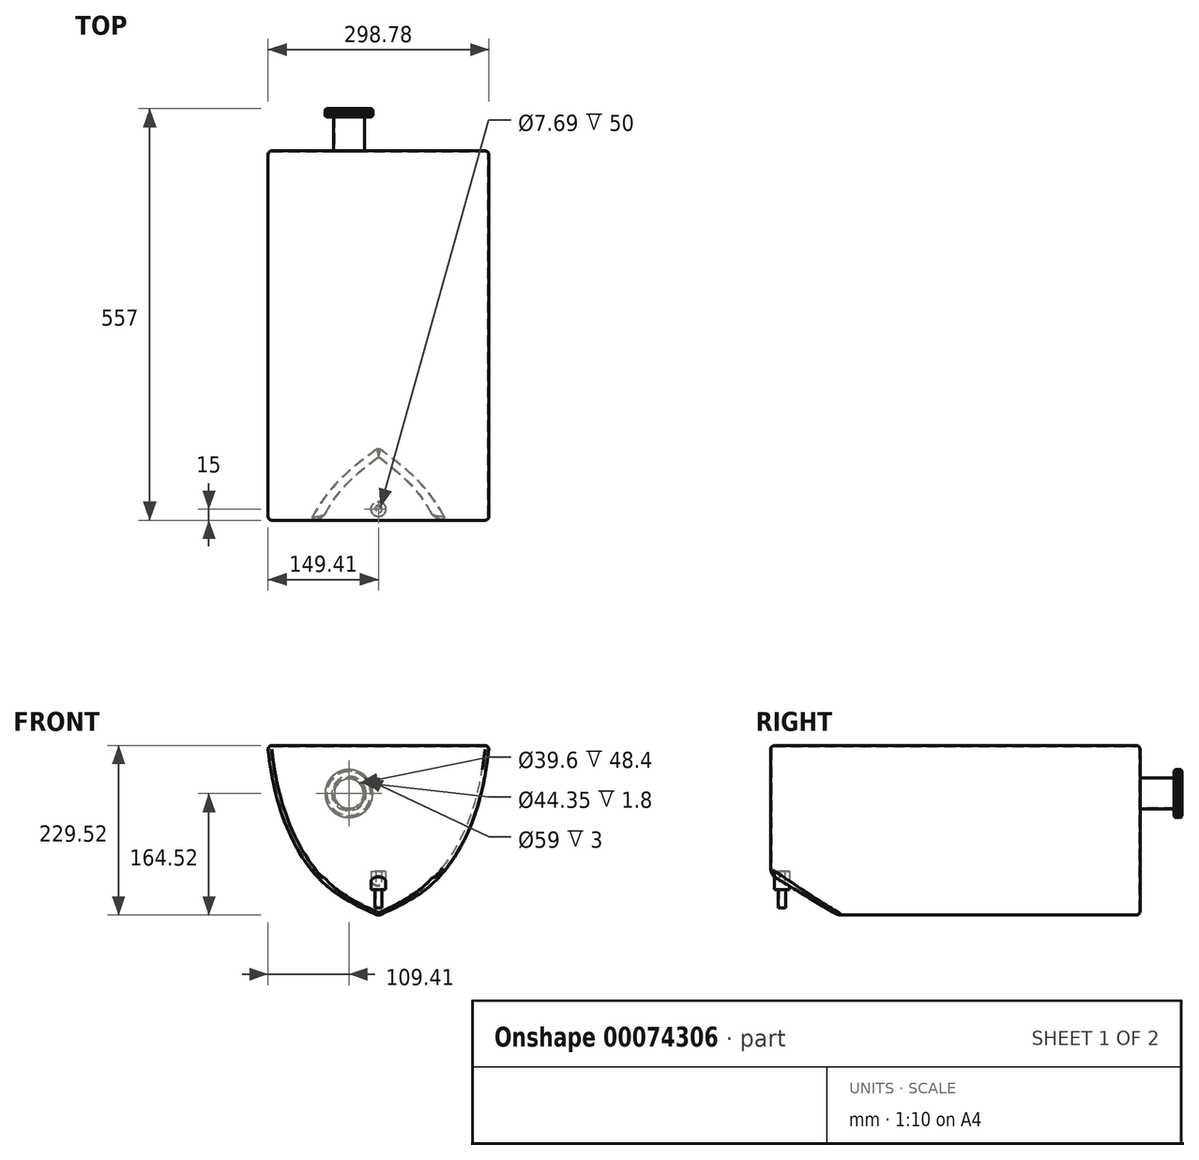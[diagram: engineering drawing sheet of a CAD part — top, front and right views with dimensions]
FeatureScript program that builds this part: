
annotation { "Feature Type Name" : "Feature", "Feature Type Description" : "" }
export const myFeature = defineFeature(function(context is Context, id is Id, definition is map)
    precondition{}
    {
        {
            var Q0;
            Q0=qCreatedBy(makeId("Front.planeOp"),FACE);
            var sketch = newSketch(context, id + "F0", { "sketchPlane" : qUnion([Q0])});
            skLineSegment(sketch, "E0", {"start": v(0, 0) * mm, "end": v(150, 0) * mm});
            skLineSegment(sketch, "E1", {"start": v(0, 0) * mm, "end": v(0, -230) * mm, "construction": true});
            skLineSegment(sketch, "E2", {"start": v(0, 0) * mm, "end": v(-150, 0) * mm});
            skLineSegment(sketch, "E3", {"start": v(-142.5, -50) * mm, "end": v(142.5, -50) * mm, "construction": true});
            skLineSegment(sketch, "E4", {"start": v(-120, -120) * mm, "end": v(120, -120) * mm, "construction": true});
            skLineSegment(sketch, "E5", {"start": v(-70, -190) * mm, "end": v(70, -190) * mm, "construction": true});
            skFitSpline(sketch, "E6", {"points": [v(0, -230) * mm, v(-70, -190) * mm, v(-120, -120) * mm, v(-142.5, -50) * mm, v(-150, 0) * mm], "startDerivative": vector(-280.35, 125.73) * mm, "endDerivative": vector(-29.97, 273.24) * mm});
            skFitSpline(sketch, "E7", {"points": [v(150, 0) * mm, v(142.5, -50) * mm, v(120, -120) * mm, v(70, -190) * mm, v(0, -230) * mm], "startDerivative": vector(-27.4, -229.65) * mm, "endDerivative": vector(-280.35, -125.73) * mm});
            skSolve(sketch);
        }
        {
            var Q0;
            Q0 = qSketchRegion(id + "F0", true);
            var Q1;
            Q1=makeQuery(id+"F0.imprint","IMPRINT",FACE,{"disambiguationData":[TD([[makeQuery(id+"F0.imprint","IMPRINT",EDGE,{"derivedFrom":sQuery(id+"F0.wireOp",EDGE,"E0")}),-1.0]])]});
            extrude(context, id + "F1", {"entities" : qUnion([Q0, Q1]), "depth" : 500 * mm});
        }
        {
            var Q0;
            Q0=makeQuery(id+"F1.opExtrude","CAP_EDGE",EDGE,{"disambiguationData":[OSD([sQuery(id+"F0.wireOp",EDGE,"E7")])],"isStart":true});
            var Q1;
            Q1=makeQuery(id+"F1.opExtrude","CAP_EDGE",EDGE,{"disambiguationData":[OSD([sQuery(id+"F0.wireOp",EDGE,"E6")])],"isStart":true});
            var Q2;
            Q2=makeQuery(id+"F1.opExtrude","SWEPT_EDGE",EDGE,{"disambiguationData":[OSD([sQuery(id+"F0.wireOp",EDGE,"E6"),sQuery(id+"F0.wireOp",EDGE,"E7")])]});
            var Q3;
            Q3=makeQuery(id+"F1.opExtrude","SWEPT_EDGE",EDGE,{"disambiguationData":[OSD([sQuery(id+"F0.wireOp",EDGE,"E2"),sQuery(id+"F0.wireOp",EDGE,"E6")])]});
            var Q4;
            Q4=makeQuery(id+"F1.opExtrude","CAP_EDGE",EDGE,{"disambiguationData":[OSD([sQuery(id+"F0.wireOp",EDGE,"E0"),sQuery(id+"F0.wireOp",EDGE,"E2")])],"isStart":true});
            var Q5;
            Q5=makeQuery(id+"F1.opExtrude","CAP_EDGE",EDGE,{"disambiguationData":[OSD([sQuery(id+"F0.wireOp",EDGE,"E7")])],"isStart":false});
            var Q6;
            Q6=makeQuery(id+"F1.opExtrude","CAP_EDGE",EDGE,{"disambiguationData":[OSD([sQuery(id+"F0.wireOp",EDGE,"E6")])],"isStart":false});
            var Q7;
            Q7=makeQuery(id+"F1.opExtrude","CAP_EDGE",EDGE,{"disambiguationData":[OSD([sQuery(id+"F0.wireOp",EDGE,"E0"),sQuery(id+"F0.wireOp",EDGE,"E2")])],"isStart":false});
            var Q8;
            Q8=makeQuery(id+"F1.opExtrude","SWEPT_EDGE",EDGE,{"disambiguationData":[OSD([sQuery(id+"F0.wireOp",EDGE,"E0"),sQuery(id+"F0.wireOp",EDGE,"E7")])]});
            fillet(context, id + "F2", {"entities" : qUnion([Q0, Q1, Q2, Q3, Q4, Q5, Q6, Q7, Q8]), "radius" : 5 * mm, "tangentPropagation" : true, "allowEdgeOverflow" : false});
        }
        {
            var Q0;
            Q0=makeQuery(id+"F0.imprint","IMPRINT",FACE,{"disambiguationData":[TD([[makeQuery(id+"F0.imprint","IMPRINT",EDGE,{"derivedFrom":sQuery(id+"F0.wireOp",EDGE,"E0")}),-1.0]])]});
            var sketch = newSketch(context, id + "F3", { "sketchPlane" : qUnion([Q0])});
            skCircle(sketch, "E8", {"center": v(-40, -65) * mm, "radius": 21 * mm});
            skSolve(sketch);
        }
        {
            var Q0;
            Q0 = qSketchRegion(id + "F3", true);
            extrude(context, id + "F4", {"entities" : qUnion([Q0]), "operationType" : NewBodyOperationType.ADD, "oppositeDirection" : true, "depth" : 46 * mm});
        }
        {
            var Q0;
            Q0=makeQuery(id+"F4.opExtrude","CAP_FACE",FACE,{"disambiguationData":[OSD([sQuery(id+"F3.wireOp",EDGE,"E8")])],"isStart":false});
            var sketch = newSketch(context, id + "F5", { "sketchPlane" : qUnion([Q0])});
            skCircle(sketch, "E9", {"center": v(40, -65) * mm, "radius": 23.38 * mm});
            skSolve(sketch);
        }
        {
            var Q0;
            Q0 = qSketchRegion(id + "F5", true);
            extrude(context, id + "F6", {"entities" : qUnion([Q0]), "operationType" : NewBodyOperationType.ADD, "depth" : 3 * mm});
        }
        {
            var Q0;
            Q0=qCreatedBy(makeId("Right.planeOp"),FACE);
            var sketch = newSketch(context, id + "F7", { "sketchPlane" : qUnion([Q0])});
            skLineSegment(sketch, "E10", {"start": v(-506.14, -175) * mm, "end": v(-466.14, -175) * mm, "construction": true});
            skLineSegment(sketch, "E11.2", {"start": v(-495, -229.08) * mm, "end": v(-5, -229.08) * mm, "construction": true});
            skFitSpline(sketch, "E12.1", {"points": [v(-500, -224.52) * mm, v(-500, -151.35) * mm, v(-500, -78.17) * mm, v(-500, -5) * mm], "construction": true});
            skLineSegment(sketch, "E13", {"start": v(-410, -168.35) * mm, "end": v(-410, -263.65) * mm, "construction": true});
            skLineSegment(sketch, "E14", {"start": v(-500, -175) * mm, "end": v(-410, -229.08) * mm});
            skLineSegment(sketch, "E15", {"start": v(-410, -229.08) * mm, "end": v(-412.5, -274.64) * mm});
            skLineSegment(sketch, "E16", {"start": v(-412.5, -274.64) * mm, "end": v(-520.63, -288.08) * mm});
            skLineSegment(sketch, "E17", {"start": v(-520.63, -288.08) * mm, "end": v(-500, -175) * mm});
            skSolve(sketch);
        }
        {
            var Q0;
            Q0 = qSketchRegion(id + "F7", true);
            extrude(context, id + "F8", {"entities" : qUnion([Q0]), "operationType" : NewBodyOperationType.REMOVE, "oppositeDirection" : true, "depth" : 500 * mm, "symmetric" : true});
        }
        {
            var Q0;
            Q0=makeQuery(id+"F8.boolean.opBoolean","INTERSECT",EDGE,{"derivedFrom":[makeQuery(id+"F1.opExtrude","SWEPT_FACE",FACE,{"disambiguationData":[OSD([sQuery(id+"F0.wireOp",EDGE,"E7")])]}),makeQuery(id+"F8.opExtrude","SWEPT_FACE",FACE,{"disambiguationData":[OSD([sQuery(id+"F7.wireOp",EDGE,"E14")])]})]});
            var Q1;
            Q1=makeQuery(id+"F8.boolean.opBoolean","INTERSECT",EDGE,{"derivedFrom":[makeQuery(id+"F1.opExtrude","SWEPT_FACE",FACE,{"disambiguationData":[OSD([sQuery(id+"F0.wireOp",EDGE,"E6")])]}),makeQuery(id+"F8.opExtrude","SWEPT_FACE",FACE,{"disambiguationData":[OSD([sQuery(id+"F7.wireOp",EDGE,"E14")])]})]});
            var Q2;
            Q2=makeQuery(id+"F8.boolean.opBoolean","COPY",EDGE,{"derivedFrom":makeQuery(id+"F8.opExtrude","SWEPT_EDGE",EDGE,{"disambiguationData":[OSD([sQuery(id+"F7.wireOp",EDGE,"E14"),sQuery(id+"F7.wireOp",EDGE,"E17")])]})});
            var Q3;
            Q3=makeQuery(id+"F8.boolean.opBoolean","COPY",EDGE,{"derivedFrom":makeQuery(id+"F8.opExtrude","SWEPT_EDGE",EDGE,{"disambiguationData":[OSD([sQuery(id+"F7.wireOp",EDGE,"E14"),sQuery(id+"F7.wireOp",EDGE,"E15")])]})});
            fillet(context, id + "F9", {"entities" : qUnion([Q0, Q1, Q2, Q3]), "radius" : 15 * mm, "tangentPropagation" : true, "allowEdgeOverflow" : false});
        }
        {
            var Q0;
            Q0=makeQuery(id+"F1.opExtrude","SWEPT_FACE",FACE,{"disambiguationData":[OSD([sQuery(id+"F0.wireOp",EDGE,"E0"),sQuery(id+"F0.wireOp",EDGE,"E2")])]});
            var sketch = newSketch(context, id + "F10", { "sketchPlane" : qUnion([Q0])});
            skCircle(sketch, "E18", {"center": v(0, -485) * mm, "radius": 10 * mm});
            skLineSegment(sketch, "E19.0", {"start": v(-144.41, -495) * mm, "end": v(144.37, -495) * mm, "construction": true});
            skSolve(sketch);
        }
        {
            var Q0;
            Q0 = qSketchRegion(id + "F10", true);
            var Q1;
            Q1=makeQuery(id+"F8.boolean.opBoolean","COPY",FACE,{"derivedFrom":makeQuery(id+"F8.opExtrude","SWEPT_FACE",FACE,{"disambiguationData":[OSD([sQuery(id+"F7.wireOp",EDGE,"E14")])]})});
            extrude(context, id + "F11", {"entities" : qUnion([Q0]), "operationType" : NewBodyOperationType.ADD, "oppositeDirection" : true, "endBoundEntityFace" : qUnion([Q1]), "depth" : 195 * mm});
        }
        {
            var Q0;
            Q0=makeQuery(id+"F11.opExtrude","CAP_FACE",FACE,{"disambiguationData":[OSD([sQuery(id+"F10.wireOp",EDGE,"E18")])],"isStart":false});
            var Q1;
            Q1=makeQuery(id+"F6.opExtrude","CAP_FACE",FACE,{"disambiguationData":[OSD([sQuery(id+"F5.wireOp",EDGE,"E9")])],"isStart":false});
            shell(context, id + "F12", {"entities" : qUnion([Q0, Q1]), "thickness" : 1.2 * mm});
        }
        {
            var Q0;
            Q0=makeQuery(id+"F11.opExtrude","CAP_FACE",FACE,{"disambiguationData":[OSD([sQuery(id+"F10.wireOp",EDGE,"E18")])],"isStart":false});
            var sketch = newSketch(context, id + "F13", { "sketchPlane" : qUnion([Q0])});
            skCircle(sketch, "E20.0", {"center": v(0, 485) * mm, "radius": 10 * mm});
            skSolve(sketch);
        }
        {
            var Q0;
            Q0 = qSketchRegion(id + "F13", true);
            extrude(context, id + "F14", {"entities" : qUnion([Q0]), "operationType" : NewBodyOperationType.ADD, "oppositeDirection" : true, "depth" : 25 * mm});
        }
        {
            var Q0;
            Q0=makeQuery(id+"F14.boolean.opBoolean","MERGE",FACE,{"derivedFrom":[makeQuery(id+"F11.opExtrude","CAP_FACE",FACE,{"disambiguationData":[OSD([sQuery(id+"F10.wireOp",EDGE,"E18")])],"isStart":false}),makeQuery(id+"F14.opExtrude","CAP_FACE",FACE,{"disambiguationData":[OSD([sQuery(id+"F13.wireOp",EDGE,"E20.0")])],"isStart":true})]});
            var sketch = newSketch(context, id + "F15", { "sketchPlane" : qUnion([Q0])});
            skCircle(sketch, "E21", {"center": v(0, 485) * mm, "radius": 5 * mm});
            skSolve(sketch);
        }
        {
            var Q0;
            Q0=makeQuery(id+"F15.imprint","IMPRINT",FACE,{"disambiguationData":[TD([[makeQuery(id+"F15.imprint","IMPRINT",EDGE,{"derivedFrom":sQuery(id+"F15.wireOp",EDGE,"E21")}),1.0]])]});
            extrude(context, id + "F16", {"entities" : qUnion([Q0]), "operationType" : NewBodyOperationType.ADD, "depth" : 25 * mm});
        }
        {
            var Q0;
            Q0=makeQuery(id+"F16.opExtrude","CAP_FACE",FACE,{"disambiguationData":[OSD([sQuery(id+"F15.wireOp",EDGE,"E21")])],"isStart":false});
            var sketch = newSketch(context, id + "F17", { "sketchPlane" : qUnion([Q0])});
            skCircle(sketch, "E22", {"center": v(0, 485) * mm, "radius": 3.84 * mm});
            skSolve(sketch);
        }
        {
            var Q0;
            Q0 = qSketchRegion(id + "F17", true);
            extrude(context, id + "F18", {"entities" : qUnion([Q0]), "operationType" : NewBodyOperationType.REMOVE, "oppositeDirection" : true, "depth" : 100 * mm});
        }
        {
            var Q0;
            Q0=makeQuery(id+"F6.opExtrude","CAP_FACE",FACE,{"disambiguationData":[OSD([sQuery(id+"F5.wireOp",EDGE,"E9")])],"isStart":false});
            var sketch = newSketch(context, id + "F19", { "sketchPlane" : qUnion([Q0])});
            skCircle(sketch, "E23", {"center": v(40, -65) * mm, "radius": 32.5 * mm});
            skSolve(sketch);
        }
        {
            var Q0;
            Q0 = qSketchRegion(id + "F19", true);
            extrude(context, id + "F20", {"entities" : qUnion([Q0]), "operationType" : NewBodyOperationType.ADD, "depth" : 8 * mm});
        }
        {
            var Q0;
            {var subQ0=sQuery(id+"F19.wireOp",EDGE,"E23");Q0=makeQuery(id+"F20.boolean.opBoolean","SPLIT",FACE,{"disambiguationData":[TD([makeQuery(id+"F6.opExtrude","SWEPT_FACE",FACE,{"disambiguationData":[OSD([sQuery(id+"F5.wireOp",EDGE,"E9")])]})])],"derivedFrom":makeQuery(id+"F20.opExtrude","CAP_FACE",FACE,{"disambiguationData":[OSD([subQ0])],"isStart":true})});}
            var sketch = newSketch(context, id + "F21", { "sketchPlane" : qUnion([Q0])});
            skCircle(sketch, "E24.0", {"center": v(-40, -65) * mm, "radius": 32.5 * mm});
            skCircle(sketch, "E25.0", {"center": v(-40, -65) * mm, "radius": 29.5 * mm});
            skSolve(sketch);
        }
        {
            var Q0;
            Q0 = qSketchRegion(id + "F21", true);
            extrude(context, id + "F22", {"entities" : qUnion([Q0]), "operationType" : NewBodyOperationType.ADD, "depth" : 3 * mm});
        }
        {
            var Q0;
            Q0=makeQuery(id+"F20.opExtrude","CAP_EDGE",EDGE,{"disambiguationData":[OSD([sQuery(id+"F19.wireOp",EDGE,"E23")])],"isStart":false});
            var Q1;
            Q1=makeQuery(id+"F22.opExtrude","CAP_EDGE",EDGE,{"disambiguationData":[OSD([sQuery(id+"F21.wireOp",EDGE,"E24.0")])],"isStart":false});
            chamfer(context, id + "F23", {"entities" : qUnion([Q0, Q1]), "width" : 2 * mm, "tangentPropagation" : true});
        }
        {
            var Q0;
            Q0=makeQuery(id+"F20.opExtrude","CAP_FACE",FACE,{"disambiguationData":[OSD([sQuery(id+"F19.wireOp",EDGE,"E23")])],"isStart":false});
            var sketch = newSketch(context, id + "F24", { "sketchPlane" : qUnion([Q0])});
            skLineSegment(sketch, "E26", {"start": v(40, -65) * mm, "end": v(64.78, -29.58) * mm, "construction": true});
            skCircle(sketch, "E27.0", {"center": v(40, -65) * mm, "radius": 32.5 * mm, "construction": true});
            skCircle(sketch, "E28", {"center": v(58.63, -38.37) * mm, "radius": 0.5 * mm});
            skSolve(sketch);
        }
        {
            var Q0;
            Q0 = qSketchRegion(id + "F24", true);
            extrude(context, id + "F25", {"entities" : qUnion([Q0]), "operationType" : NewBodyOperationType.REMOVE, "oppositeDirection" : true, "depth" : 25 * mm});
        }
        {
            var Q0;
            Q0=makeQuery(id+"F25.boolean.opBoolean","COPY",FACE,{"derivedFrom":makeQuery(id+"F25.opExtrude","SWEPT_FACE",FACE,{"disambiguationData":[OSD([sQuery(id+"F24.wireOp",EDGE,"E28")])]})});
            var Q1;
            {var subQ0=sQuery(id+"F19.wireOp",EDGE,"E23");Q1=makeQuery(id+"F23.opChamfer","BLEND_EDGE",EDGE,{"blendedFrom":[makeQuery(id+"F20.opExtrude","CAP_EDGE",EDGE,{"disambiguationData":[OSD([subQ0])],"isStart":false}),makeQuery(id+"F20.opExtrude","CAP_FACE",FACE,{"disambiguationData":[OSD([subQ0])],"isStart":false})],"blendedInto":[makeQuery(id+"F20.opExtrude","CAP_FACE",FACE,{"disambiguationData":[OSD([subQ0])],"isStart":false})]});}
            circularPattern(context, id + "F26", {"patternType" : PatternType.FACE, "faces" : qUnion([Q0]), "axis" : qUnion([Q1]), "angle" : 360 * degree, "instanceCount" : 72, "equalSpace" : true});
        }
    });
